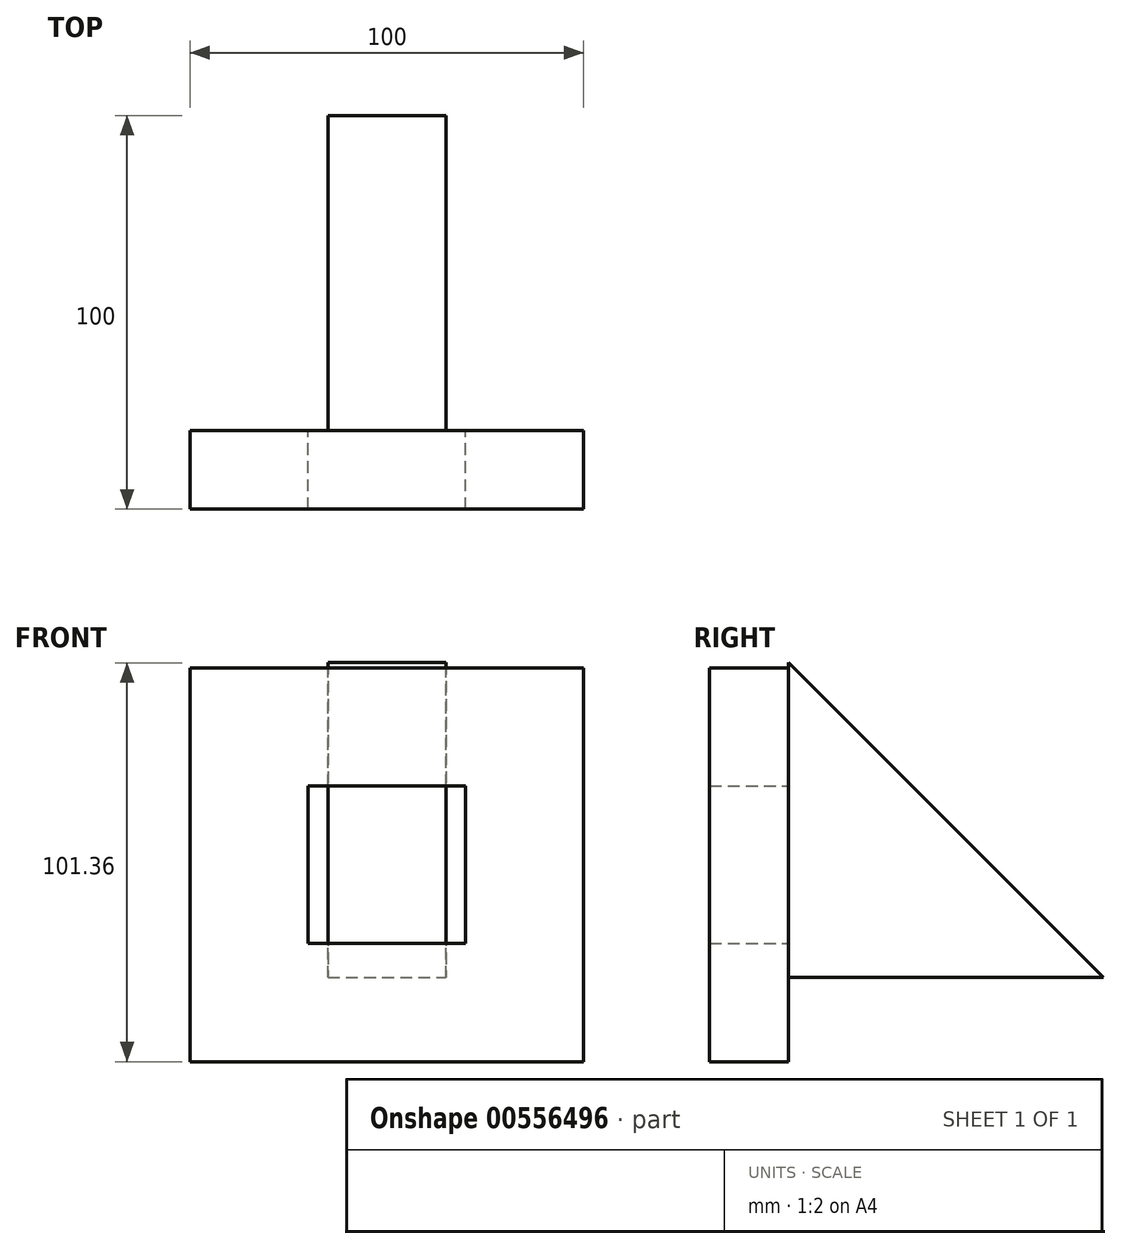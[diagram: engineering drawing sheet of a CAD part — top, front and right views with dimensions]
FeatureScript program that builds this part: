
annotation { "Feature Type Name" : "Feature", "Feature Type Description" : "" }
export const myFeature = defineFeature(function(context is Context, id is Id, definition is map)
    precondition{}
    {
        {
            var Q0;
            Q0=qCreatedBy(makeId("Front.planeOp"),FACE);
            var sketch = newSketch(context, id + "F0", { "sketchPlane" : qUnion([Q0])});
            skLineSegment(sketch, "E0.bottom", {"start": v(50, 50) * mm, "end": v(-50, 50) * mm});
            skLineSegment(sketch, "E0.top", {"start": v(50, -50) * mm, "end": v(-50, -50) * mm});
            skLineSegment(sketch, "E0.left", {"start": v(50, 50) * mm, "end": v(50, -50) * mm});
            skLineSegment(sketch, "E0.right", {"start": v(-50, 50) * mm, "end": v(-50, -50) * mm});
            skPoint(sketch, "E0.middle", {"position": v(0, 0) * mm});
            skLineSegment(sketch, "E1.bottom", {"start": v(20, 20) * mm, "end": v(-20, 20) * mm});
            skLineSegment(sketch, "E1.top", {"start": v(20, -20) * mm, "end": v(-20, -20) * mm});
            skLineSegment(sketch, "E1.left", {"start": v(20, 20) * mm, "end": v(20, -20) * mm});
            skLineSegment(sketch, "E1.right", {"start": v(-20, 20) * mm, "end": v(-20, -20) * mm});
            skSolve(sketch);
        }
        {
            var Q0;
            Q0=makeQuery(id+"F0.imprint","IMPRINT",FACE,{"disambiguationData":[TD([[makeQuery(id+"F0.imprint","IMPRINT",EDGE,{"derivedFrom":sQuery(id+"F0.wireOp",EDGE,"E0.bottom")}),1.0]])]});
            extrude(context, id + "F1", {"entities" : qUnion([Q0]), "depth" : 20 * mm, "offsetDistance" : 25 * mm});
        }
        {
            var Q0;
            Q0=qCreatedBy(makeId("Right.planeOp"),FACE);
            var sketch = newSketch(context, id + "F2", { "sketchPlane" : qUnion([Q0])});
            skLineSegment(sketch, "E2", {"start": v(0, 51.36) * mm, "end": v(80, -28.64) * mm});
            skLineSegment(sketch, "E3", {"start": v(80, -28.64) * mm, "end": v(0, -28.64) * mm});
            skLineSegment(sketch, "E4", {"start": v(0, -28.64) * mm, "end": v(0, 51.36) * mm});
            skSolve(sketch);
        }
        {
            var Q0;
            Q0=makeQuery(id+"F2.imprint","IMPRINT",FACE,{"disambiguationData":[TD([[makeQuery(id+"F2.imprint","IMPRINT",EDGE,{"derivedFrom":sQuery(id+"F2.wireOp",EDGE,"E2")}),-1.0]])]});
            extrude(context, id + "F3", {"entities" : qUnion([Q0]), "operationType" : NewBodyOperationType.ADD, "endBound" : BoundingType.SYMMETRIC, "oppositeDirection" : true, "depth" : 30 * mm, "offsetDistance" : 25 * mm});
        }
    });
